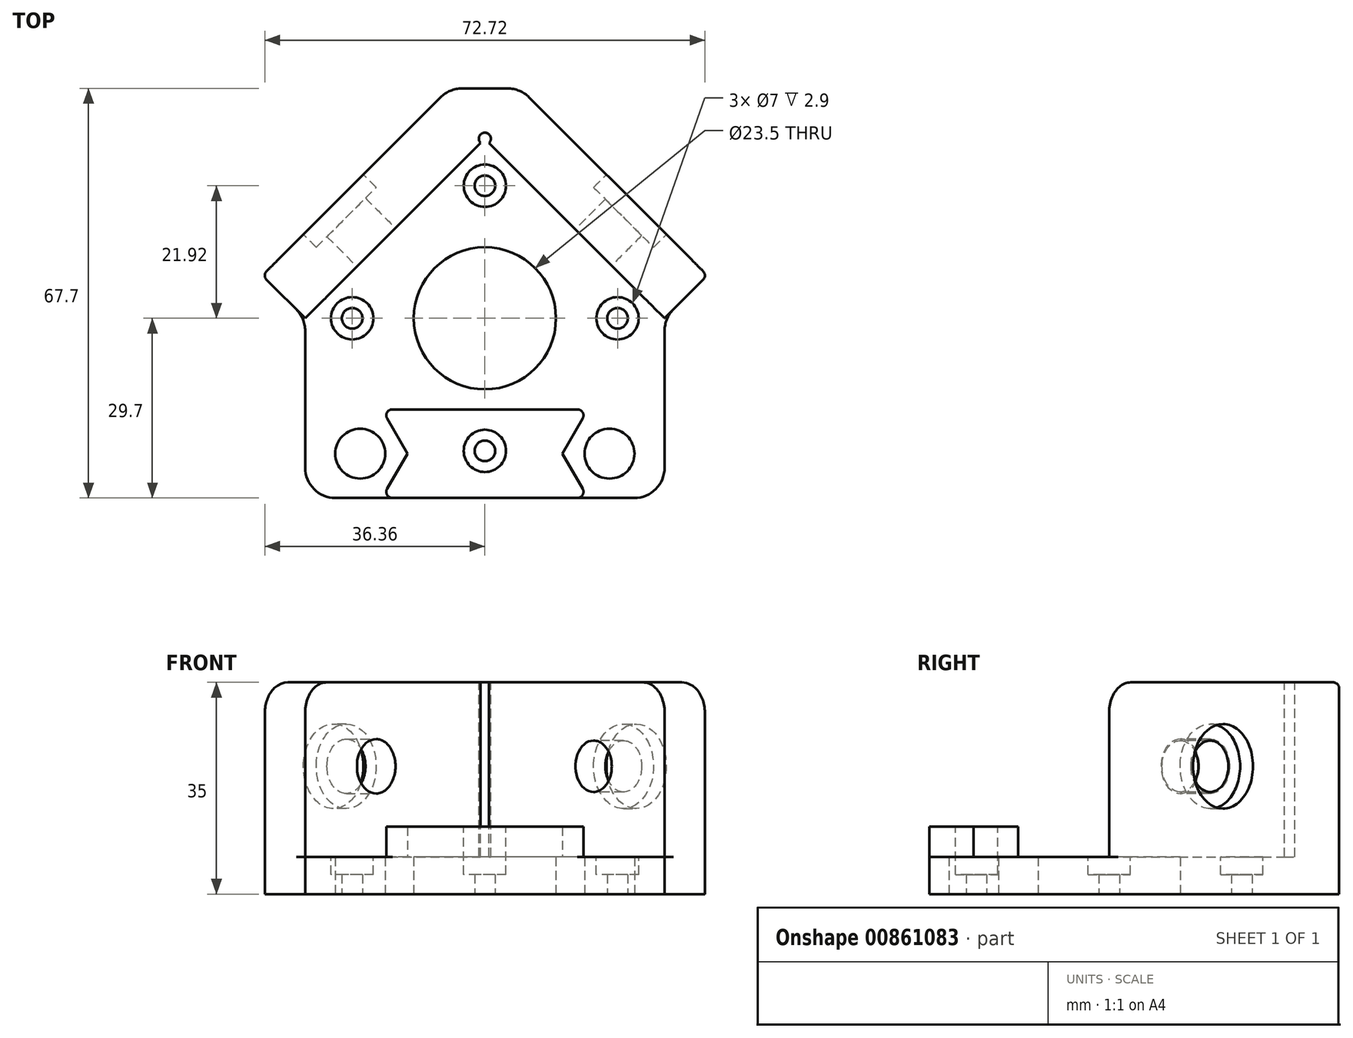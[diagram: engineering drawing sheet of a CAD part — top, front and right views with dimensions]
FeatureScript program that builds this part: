
annotation { "Feature Type Name" : "Feature", "Feature Type Description" : "" }
export const myFeature = defineFeature(function(context is Context, id is Id, definition is map)
    precondition{}
    {
        {
            var Q0;
            Q0=qCreatedBy(makeId("Top.planeOp"),FACE);
            var sketch = newSketch(context, id + "F0", { "sketchPlane" : qUnion([Q0])});
            skLineSegment(sketch, "E0", {"start": v(0, 0) * mm, "end": v(-29.7, 0) * mm});
            skLineSegment(sketch, "E1", {"start": v(-29.7, 0) * mm, "end": v(-29.7, 29.7) * mm});
            skLineSegment(sketch, "E2", {"start": v(-29.7, 29.7) * mm, "end": v(0, 59.4) * mm});
            skLineSegment(sketch, "E3", {"start": v(0, 59.4) * mm, "end": v(0, 0) * mm, "construction": true});
            skLineSegment(sketch, "E4", {"start": v(-29.7, 7.78) * mm, "end": v(0, 7.78) * mm, "construction": true});
            skCircle(sketch, "E5", {"center": v(0, 29.7) * mm, "radius": 11.75 * mm});
            skLineSegment(sketch, "E6", {"start": v(0, 29.7) * mm, "end": v(0, 59.4) * mm, "construction": true});
            skLineSegment(sketch, "E7", {"start": v(0, 59.4) * mm, "end": v(-29.7, 29.7) * mm, "construction": true});
            skLineSegment(sketch, "E8", {"start": v(-29.7, 29.7) * mm, "end": v(0, 0) * mm, "construction": true});
            skLineSegment(sketch, "E9", {"start": v(0, 51.62) * mm, "end": v(-21.92, 29.7) * mm, "construction": true});
            skLineSegment(sketch, "E10", {"start": v(-21.92, 29.7) * mm, "end": v(0, 7.78) * mm, "construction": true});
            skCircle(sketch, "E11", {"center": v(-20.59, 7.32) * mm, "radius": 4.12 * mm});
            skCircle(sketch, "E12", {"center": v(-21.92, 29.7) * mm, "radius": 1.7 * mm});
            skCircle(sketch, "E13", {"center": v(0, 51.62) * mm, "radius": 1.7 * mm});
            skCircle(sketch, "E14", {"center": v(0, 7.78) * mm, "radius": 1.7 * mm});
            skLineSegment(sketch, "E15.MirrorCS", {"start": v(29.7, 29.7) * mm, "end": v(0, 59.4) * mm});
            skLineSegment(sketch, "E16.MirrorCS", {"start": v(0, 0) * mm, "end": v(29.7, 0) * mm});
            skLineSegment(sketch, "E17.MirrorCS", {"start": v(29.7, 0) * mm, "end": v(29.7, 29.7) * mm});
            skLineSegment(sketch, "E18.MirrorCS", {"start": v(29.7, 7.78) * mm, "end": v(0, 7.78) * mm, "construction": true});
            skCircle(sketch, "E19.MirrorC", {"center": v(21.92, 29.7) * mm, "radius": 1.7 * mm});
            skCircle(sketch, "E20.MirrorC", {"center": v(20.6, 7.32) * mm, "radius": 4.12 * mm});
            skLineSegment(sketch, "E21.MirrorCS", {"start": v(0, 59.4) * mm, "end": v(29.7, 29.7) * mm, "construction": true});
            skLineSegment(sketch, "E22.MirrorCS", {"start": v(0, 51.62) * mm, "end": v(21.92, 29.7) * mm, "construction": true});
            skLineSegment(sketch, "E23.MirrorCS", {"start": v(21.92, 29.7) * mm, "end": v(0, 7.78) * mm, "construction": true});
            skLineSegment(sketch, "E24.MirrorCS", {"start": v(29.7, 29.7) * mm, "end": v(0, 0) * mm, "construction": true});
            skSolve(sketch);
        }
        {
            var Q0;
            Q0=qSketchRegion(id+"F0",true);
            extrude(context, id + "F1", {"entities" : qUnion([Q0]), "depth" : 6.13 * mm, "offsetDistance" : 25 * mm});
        }
        {
            var Q0;
            Q0=makeQuery(id+"F1.opExtrude","CAP_FACE",FACE,{"disambiguationData":[OSD([sQuery(id+"F0.wireOp",EDGE,"E0"),sQuery(id+"F0.wireOp",EDGE,"E1"),sQuery(id+"F0.wireOp",EDGE,"E2"),sQuery(id+"F0.wireOp",EDGE,"E5"),sQuery(id+"F0.wireOp",EDGE,"E11"),sQuery(id+"F0.wireOp",EDGE,"E12"),sQuery(id+"F0.wireOp",EDGE,"E15.MirrorCS"),sQuery(id+"F0.wireOp",EDGE,"E16.MirrorCS"),sQuery(id+"F0.wireOp",EDGE,"E17.MirrorCS"),sQuery(id+"F0.wireOp",EDGE,"E14"),sQuery(id+"F0.wireOp",EDGE,"E13"),sQuery(id+"F0.wireOp",EDGE,"E19.MirrorC"),sQuery(id+"F0.wireOp",EDGE,"E20.MirrorC")])],"isStart":true});
            var sketch = newSketch(context, id + "F2", { "sketchPlane" : qUnion([Q0])});
            skLineSegment(sketch, "E25", {"start": v(-29.7, -29.7) * mm, "end": v(-36.77, -36.77) * mm});
            skLineSegment(sketch, "E26", {"start": v(-36.77, -36.77) * mm, "end": v(-5.84, -67.7) * mm});
            skLineSegment(sketch, "E27", {"start": v(-5.84, -67.7) * mm, "end": v(0, -67.7) * mm});
            skLineSegment(sketch, "E28", {"start": v(0, -29.7) * mm, "end": v(-11.75, -29.7) * mm, "construction": true});
            skLineSegment(sketch, "E29", {"start": v(0, -67.7) * mm, "end": v(0, -29.7) * mm, "construction": true});
            skLineSegment(sketch, "E30.MirrorCS", {"start": v(0, -29.7) * mm, "end": v(11.75, -29.7) * mm, "construction": true});
            skLineSegment(sketch, "E31.MirrorCS", {"start": v(5.84, -67.7) * mm, "end": v(0, -67.7) * mm});
            skLineSegment(sketch, "E32.MirrorCS", {"start": v(36.77, -36.77) * mm, "end": v(5.84, -67.7) * mm});
            skLineSegment(sketch, "E33.MirrorCS", {"start": v(29.7, -29.7) * mm, "end": v(36.77, -36.77) * mm});
            skLineSegment(sketch, "E34", {"start": v(-29.7, -29.7) * mm, "end": v(0, -59.4) * mm});
            skLineSegment(sketch, "E35", {"start": v(0, -59.4) * mm, "end": v(29.7, -29.7) * mm});
            skSolve(sketch);
        }
        {
            var Q0;
            Q0=qSketchRegion(id+"F2",true);
            extrude(context, id + "F3", {"entities" : qUnion([Q0]), "operationType" : NewBodyOperationType.ADD, "oppositeDirection" : true, "depth" : 35 * mm, "offsetDistance" : 25 * mm});
        }
        {
            var Q0;
            Q0=makeQuery(id+"F3.opExtrude","SWEPT_FACE",FACE,{"disambiguationData":[OSD([sQuery(id+"F2.wireOp",EDGE,"E34")])]});
            var sketch = newSketch(context, id + "F4", { "sketchPlane" : qUnion([Q0])});
            skCircle(sketch, "E36", {"center": v(16.6, 21.13) * mm, "radius": 4.5 * mm});
            skLineSegment(sketch, "E37", {"start": v(42, 6.13) * mm, "end": v(-8.8, 6.13) * mm, "construction": true});
            skLineSegment(sketch, "E38", {"start": v(16.6, 6.13) * mm, "end": v(16.6, 35) * mm, "construction": true});
            skSolve(sketch);
        }
        {
            var Q0;
            Q0=qSketchRegion(id+"F4",true);
            extrude(context, id + "F5", {"entities" : qUnion([Q0]), "operationType" : NewBodyOperationType.REMOVE, "endBound" : BoundingType.UP_TO_NEXT, "oppositeDirection" : true, "depth" : 25 * mm, "offsetDistance" : 25 * mm});
        }
        {
            var Q0;
            Q0=makeQuery(id+"F3.opExtrude","SWEPT_FACE",FACE,{"disambiguationData":[OSD([sQuery(id+"F2.wireOp",EDGE,"E35")])]});
            var sketch = newSketch(context, id + "F6", { "sketchPlane" : qUnion([Q0])});
            skLineSegment(sketch, "E39", {"start": v(-42, 6.13) * mm, "end": v(8.8, 6.13) * mm, "construction": true});
            skLineSegment(sketch, "E40", {"start": v(-16.6, 6.13) * mm, "end": v(-16.6, 35) * mm, "construction": true});
            skCircle(sketch, "E41", {"center": v(-16.6, 21.13) * mm, "radius": 4.25 * mm});
            skSolve(sketch);
        }
        {
            var Q0;
            Q0=qSketchRegion(id+"F6",true);
            extrude(context, id + "F7", {"entities" : qUnion([Q0]), "operationType" : NewBodyOperationType.REMOVE, "endBound" : BoundingType.UP_TO_NEXT, "oppositeDirection" : true, "depth" : 25 * mm, "offsetDistance" : 25 * mm});
        }
        {
            var Q0;
            Q0=makeQuery(id+"F3.opExtrude","SWEPT_FACE",FACE,{"disambiguationData":[OSD([sQuery(id+"F2.wireOp",EDGE,"E26")])]});
            var sketch = newSketch(context, id + "F8", { "sketchPlane" : qUnion([Q0])});
            skCircle(sketch, "E42", {"center": v(-16.6, 21.13) * mm, "radius": 7 * mm});
            skSolve(sketch);
        }
        {
            var Q0;
            Q0=qSketchRegion(id+"F8",true);
            extrude(context, id + "F9", {"entities" : qUnion([Q0]), "operationType" : NewBodyOperationType.REMOVE, "oppositeDirection" : true, "depth" : 3 * mm, "offsetDistance" : 25 * mm});
        }
        {
            var Q0;
            Q0=makeQuery(id+"F3.opExtrude","SWEPT_FACE",FACE,{"disambiguationData":[OSD([sQuery(id+"F2.wireOp",EDGE,"E32.MirrorCS")])]});
            var sketch = newSketch(context, id + "F10", { "sketchPlane" : qUnion([Q0])});
            skCircle(sketch, "E43", {"center": v(16.6, 21.13) * mm, "radius": 7 * mm});
            skSolve(sketch);
        }
        {
            var Q0;
            Q0=qSketchRegion(id+"F10",true);
            extrude(context, id + "F11", {"entities" : qUnion([Q0]), "operationType" : NewBodyOperationType.REMOVE, "oppositeDirection" : true, "depth" : 3 * mm, "offsetDistance" : 25 * mm});
        }
        {
            var Q0;
            Q0=makeQuery(id+"F1.opExtrude","CAP_FACE",FACE,{"disambiguationData":[OSD([sQuery(id+"F0.wireOp",EDGE,"E0"),sQuery(id+"F0.wireOp",EDGE,"E1"),sQuery(id+"F0.wireOp",EDGE,"E2"),sQuery(id+"F0.wireOp",EDGE,"E5"),sQuery(id+"F0.wireOp",EDGE,"E11"),sQuery(id+"F0.wireOp",EDGE,"E12"),sQuery(id+"F0.wireOp",EDGE,"E15.MirrorCS"),sQuery(id+"F0.wireOp",EDGE,"E16.MirrorCS"),sQuery(id+"F0.wireOp",EDGE,"E17.MirrorCS"),sQuery(id+"F0.wireOp",EDGE,"E14"),sQuery(id+"F0.wireOp",EDGE,"E13"),sQuery(id+"F0.wireOp",EDGE,"E19.MirrorC"),sQuery(id+"F0.wireOp",EDGE,"E20.MirrorC")])],"isStart":false});
            var sketch = newSketch(context, id + "F12", { "sketchPlane" : qUnion([Q0])});
            skCircle(sketch, "E44", {"center": v(0, 51.62) * mm, "radius": 3.5 * mm});
            skCircle(sketch, "E45", {"center": v(-21.92, 29.7) * mm, "radius": 3.5 * mm});
            skCircle(sketch, "E46", {"center": v(21.92, 29.7) * mm, "radius": 3.5 * mm});
            skCircle(sketch, "E47", {"center": v(0, 7.78) * mm, "radius": 3.5 * mm});
            skSolve(sketch);
        }
        {
            var Q0;
            Q0=makeQuery(id+"F3.opExtrude","CAP_EDGE",EDGE,{"disambiguationData":[OSD([sQuery(id+"F2.wireOp",EDGE,"E33.MirrorCS")])],"isStart":false});
            var Q1;
            Q1=makeQuery(id+"F3.opExtrude","CAP_EDGE",EDGE,{"disambiguationData":[OSD([sQuery(id+"F2.wireOp",EDGE,"E25")])],"isStart":false});
            var Q2;
            {var subQ0=sQuery(id+"F0.wireOp",EDGE,"E17.MirrorCS");Q2=makeQuery(id+"F3.boolean.opBoolean","MERGE",EDGE,{"derivedFrom":[makeQuery(id+"F1.opExtrude","SWEPT_EDGE",EDGE,{"disambiguationData":[OSD([sQuery(id+"F0.wireOp",EDGE,"E15.MirrorCS"),subQ0])]}),makeQuery(id+"F3.opExtrude","SWEPT_EDGE",EDGE,{"disambiguationData":[OSD([subQ0,sQuery(id+"F2.wireOp",EDGE,"E33.MirrorCS"),sQuery(id+"F2.wireOp",EDGE,"E35")])]})]});}
            var Q3;
            Q3=makeQuery(id+"F1.opExtrude","SWEPT_EDGE",EDGE,{"disambiguationData":[OSD([sQuery(id+"F0.wireOp",EDGE,"E16.MirrorCS"),sQuery(id+"F0.wireOp",EDGE,"E17.MirrorCS")])]});
            var Q4;
            Q4=makeQuery(id+"F1.opExtrude","SWEPT_EDGE",EDGE,{"disambiguationData":[OSD([sQuery(id+"F0.wireOp",EDGE,"E0"),sQuery(id+"F0.wireOp",EDGE,"E1")])]});
            var Q5;
            {var subQ0=sQuery(id+"F0.wireOp",EDGE,"E1");Q5=makeQuery(id+"F3.boolean.opBoolean","MERGE",EDGE,{"derivedFrom":[makeQuery(id+"F1.opExtrude","SWEPT_EDGE",EDGE,{"disambiguationData":[OSD([subQ0,sQuery(id+"F0.wireOp",EDGE,"E2")])]}),makeQuery(id+"F3.opExtrude","SWEPT_EDGE",EDGE,{"disambiguationData":[OSD([subQ0,sQuery(id+"F2.wireOp",EDGE,"E25"),sQuery(id+"F2.wireOp",EDGE,"E34")])]})]});}
            var Q6;
            Q6=makeQuery(id+"F3.opExtrude","SWEPT_EDGE",EDGE,{"disambiguationData":[OSD([sQuery(id+"F2.wireOp",EDGE,"E26"),sQuery(id+"F2.wireOp",EDGE,"E27")])]});
            var Q7;
            Q7=makeQuery(id+"F3.opExtrude","SWEPT_EDGE",EDGE,{"disambiguationData":[OSD([sQuery(id+"F2.wireOp",EDGE,"E31.MirrorCS"),sQuery(id+"F2.wireOp",EDGE,"E32.MirrorCS")])]});
            fillet(context, id + "F13", {"entities" : qUnion([Q0, Q1, Q2, Q3, Q4, Q5, Q6, Q7]), "radius" : 5 * mm, "tangentPropagation" : true, "allowEdgeOverflow" : false});
        }
        {
            var Q0;
            Q0=qSketchRegion(id+"F12",true);
            extrude(context, id + "F14", {"entities" : qUnion([Q0]), "operationType" : NewBodyOperationType.REMOVE, "oppositeDirection" : true, "depth" : 2.9 * mm, "offsetDistance" : 25 * mm});
        }
        {
            var Q0;
            Q0=makeQuery(id+"F1.opExtrude","CAP_FACE",FACE,{"disambiguationData":[OSD([sQuery(id+"F0.wireOp",EDGE,"E0"),sQuery(id+"F0.wireOp",EDGE,"E1"),sQuery(id+"F0.wireOp",EDGE,"E2"),sQuery(id+"F0.wireOp",EDGE,"E5"),sQuery(id+"F0.wireOp",EDGE,"E11"),sQuery(id+"F0.wireOp",EDGE,"E12"),sQuery(id+"F0.wireOp",EDGE,"E15.MirrorCS"),sQuery(id+"F0.wireOp",EDGE,"E16.MirrorCS"),sQuery(id+"F0.wireOp",EDGE,"E17.MirrorCS"),sQuery(id+"F0.wireOp",EDGE,"E14"),sQuery(id+"F0.wireOp",EDGE,"E13"),sQuery(id+"F0.wireOp",EDGE,"E19.MirrorC"),sQuery(id+"F0.wireOp",EDGE,"E20.MirrorC")])],"isStart":false});
            var sketch = newSketch(context, id + "F15", { "sketchPlane" : qUnion([Q0])});
            skCircle(sketch, "E48.cCircle", {"center": v(-20.59, 7.32) * mm, "radius": 6.75 * mm, "construction": true});
            skLineSegment(sketch, "E48.0", {"start": v(-16.7, 14.07) * mm, "end": v(-12.8, 7.32) * mm});
            skLineSegment(sketch, "E48.1", {"start": v(-12.8, 7.32) * mm, "end": v(-16.7, 0.57) * mm});
            skLineSegment(sketch, "E48.2", {"start": v(-16.7, 0.57) * mm, "end": v(-24.49, 0.57) * mm});
            skLineSegment(sketch, "E48.3", {"start": v(-24.49, 0.57) * mm, "end": v(-28.38, 7.32) * mm});
            skLineSegment(sketch, "E48.4", {"start": v(-28.38, 7.32) * mm, "end": v(-24.49, 14.07) * mm});
            skLineSegment(sketch, "E48.5", {"start": v(-24.49, 14.07) * mm, "end": v(-16.7, 14.07) * mm});
            skPoint(sketch, "E48.0.midPoint", {"position": v(-14.74, 10.7) * mm});
            skLineSegment(sketch, "E49", {"start": v(0, 59.4) * mm, "end": v(0, 0) * mm, "construction": true});
            skLineSegment(sketch, "E50.MirrorCS", {"start": v(24.49, 14.07) * mm, "end": v(16.7, 14.07) * mm});
            skLineSegment(sketch, "E51.MirrorCS", {"start": v(16.7, 14.07) * mm, "end": v(12.8, 7.32) * mm});
            skLineSegment(sketch, "E52.MirrorCS", {"start": v(28.38, 7.32) * mm, "end": v(24.49, 14.07) * mm});
            skCircle(sketch, "E53.MirrorC", {"center": v(20.59, 7.32) * mm, "radius": 6.75 * mm, "construction": true});
            skLineSegment(sketch, "E54.MirrorCS", {"start": v(24.49, 0.57) * mm, "end": v(28.38, 7.32) * mm});
            skLineSegment(sketch, "E55.MirrorCS", {"start": v(12.8, 7.32) * mm, "end": v(16.7, 0.57) * mm});
            skLineSegment(sketch, "E56.MirrorCS", {"start": v(16.7, 0.57) * mm, "end": v(24.49, 0.57) * mm});
            skPoint(sketch, "E57.MirrorP", {"position": v(14.74, 10.7) * mm});
            skLineSegment(sketch, "E58", {"start": v(-16.7, 14.07) * mm, "end": v(16.7, 14.07) * mm});
            skLineSegment(sketch, "E59", {"start": v(-16.7, 0.57) * mm, "end": v(16.7, 0.57) * mm});
            skCircle(sketch, "E60", {"center": v(0, 7.78) * mm, "radius": 3.5 * mm});
            skLineSegment(sketch, "E61", {"start": v(-16.7, 0.57) * mm, "end": v(-17.02, 0) * mm});
            skLineSegment(sketch, "E62", {"start": v(-17.02, 0) * mm, "end": v(0, 0) * mm});
            skLineSegment(sketch, "E63.MirrorCS", {"start": v(16.7, 0.57) * mm, "end": v(17.02, 0) * mm});
            skLineSegment(sketch, "E64.MirrorCS", {"start": v(17.02, 0) * mm, "end": v(0, 0) * mm});
            skLineSegment(sketch, "E65", {"start": v(-12.8, 7.32) * mm, "end": v(12.8, 7.32) * mm, "construction": true});
            skLineSegment(sketch, "E66.MirrorCS", {"start": v(-16.7, 14.07) * mm, "end": v(-17.02, 14.64) * mm});
            skLineSegment(sketch, "E67.MirrorCS", {"start": v(16.7, 14.07) * mm, "end": v(17.02, 14.64) * mm});
            skLineSegment(sketch, "E68.MirrorCS", {"start": v(-17.02, 14.64) * mm, "end": v(0, 14.64) * mm});
            skLineSegment(sketch, "E69.MirrorCS", {"start": v(17.02, 14.64) * mm, "end": v(0, 14.64) * mm});
            skSolve(sketch);
        }
        {
            var Q0;
            Q0=makeQuery(id+"F15.imprint","IMPRINT",FACE,{"disambiguationData":[TD([[makeQuery(id+"F15.imprint","IMPRINT",EDGE,{"derivedFrom":sQuery(id+"F15.wireOp",EDGE,"E48.0")}),1.0]])]});
            var Q1;
            Q1=makeQuery(id+"F15.imprint","IMPRINT",FACE,{"disambiguationData":[TD([[makeQuery(id+"F15.imprint","IMPRINT",EDGE,{"derivedFrom":sQuery(id+"F15.wireOp",EDGE,"E59")}),-1.0]])]});
            var Q2;
            Q2=makeQuery(id+"F15.imprint","IMPRINT",FACE,{"disambiguationData":[TD([[makeQuery(id+"F15.imprint","IMPRINT",EDGE,{"derivedFrom":sQuery(id+"F15.wireOp",EDGE,"E66.MirrorCS")}),-1.0]])]});
            extrude(context, id + "F16", {"entities" : qUnion([Q0, Q1, Q2]), "operationType" : NewBodyOperationType.ADD, "depth" : 5 * mm, "offsetDistance" : 25 * mm});
        }
        {
            var Q0;
            Q0=makeQuery(id+"F3.opExtrude","SWEPT_EDGE",EDGE,{"disambiguationData":[OSD([sQuery(id+"F2.wireOp",EDGE,"E32.MirrorCS"),sQuery(id+"F2.wireOp",EDGE,"E33.MirrorCS")])]});
            var Q1;
            Q1=makeQuery(id+"F16.opExtrude","SWEPT_EDGE",EDGE,{"disambiguationData":[OSD([sQuery(id+"F0.wireOp",EDGE,"E0"),sQuery(id+"F0.wireOp",EDGE,"E16.MirrorCS"),sQuery(id+"F15.wireOp",EDGE,"E61"),sQuery(id+"F15.wireOp",EDGE,"E62")])]});
            var Q2;
            Q2=makeQuery(id+"F16.opExtrude","SWEPT_EDGE",EDGE,{"disambiguationData":[OSD([sQuery(id+"F15.wireOp",EDGE,"E66.MirrorCS"),sQuery(id+"F15.wireOp",EDGE,"E68.MirrorCS")])]});
            var Q3;
            Q3=makeQuery(id+"F16.opExtrude","SWEPT_EDGE",EDGE,{"disambiguationData":[OSD([sQuery(id+"F15.wireOp",EDGE,"E67.MirrorCS"),sQuery(id+"F15.wireOp",EDGE,"E69.MirrorCS")])]});
            var Q4;
            Q4=makeQuery(id+"F16.opExtrude","SWEPT_EDGE",EDGE,{"disambiguationData":[OSD([sQuery(id+"F0.wireOp",EDGE,"E0"),sQuery(id+"F0.wireOp",EDGE,"E16.MirrorCS"),sQuery(id+"F15.wireOp",EDGE,"E63.MirrorCS"),sQuery(id+"F15.wireOp",EDGE,"E64.MirrorCS")])]});
            fillet(context, id + "F17", {"entities" : qUnion([Q0, Q1, Q2, Q3, Q4]), "radius" : 1 * mm, "tangentPropagation" : true, "allowEdgeOverflow" : false});
        }
        {
            var Q0;
            Q0=makeQuery(id+"F3.opExtrude","CAP_FACE",FACE,{"disambiguationData":[OSD([sQuery(id+"F2.wireOp",EDGE,"E25"),sQuery(id+"F2.wireOp",EDGE,"E26"),sQuery(id+"F2.wireOp",EDGE,"E27"),sQuery(id+"F2.wireOp",EDGE,"E31.MirrorCS"),sQuery(id+"F2.wireOp",EDGE,"E32.MirrorCS"),sQuery(id+"F2.wireOp",EDGE,"E33.MirrorCS"),sQuery(id+"F2.wireOp",EDGE,"E34"),sQuery(id+"F2.wireOp",EDGE,"E35")])],"isStart":false});
            var sketch = newSketch(context, id + "F18", { "sketchPlane" : qUnion([Q0])});
            skCircle(sketch, "E70", {"center": v(0, 59.4) * mm, "radius": 1 * mm});
            skSolve(sketch);
        }
        {
            var Q0;
            Q0=qSketchRegion(id+"F18",true);
            var Q1;
            Q1=makeQuery(id+"F1.opExtrude","CAP_FACE",FACE,{"disambiguationData":[OSD([sQuery(id+"F0.wireOp",EDGE,"E0"),sQuery(id+"F0.wireOp",EDGE,"E1"),sQuery(id+"F0.wireOp",EDGE,"E2"),sQuery(id+"F0.wireOp",EDGE,"E5"),sQuery(id+"F0.wireOp",EDGE,"E11"),sQuery(id+"F0.wireOp",EDGE,"E12"),sQuery(id+"F0.wireOp",EDGE,"E15.MirrorCS"),sQuery(id+"F0.wireOp",EDGE,"E16.MirrorCS"),sQuery(id+"F0.wireOp",EDGE,"E17.MirrorCS"),sQuery(id+"F0.wireOp",EDGE,"E14"),sQuery(id+"F0.wireOp",EDGE,"E13"),sQuery(id+"F0.wireOp",EDGE,"E19.MirrorC"),sQuery(id+"F0.wireOp",EDGE,"E20.MirrorC")])],"isStart":false});
            extrude(context, id + "F19", {"entities" : qUnion([Q0]), "operationType" : NewBodyOperationType.REMOVE, "endBound" : BoundingType.UP_TO_SURFACE, "oppositeDirection" : true, "depth" : 25 * mm, "endBoundEntityFace" : qUnion([Q1]), "offsetDistance" : 25 * mm});
        }
    });
